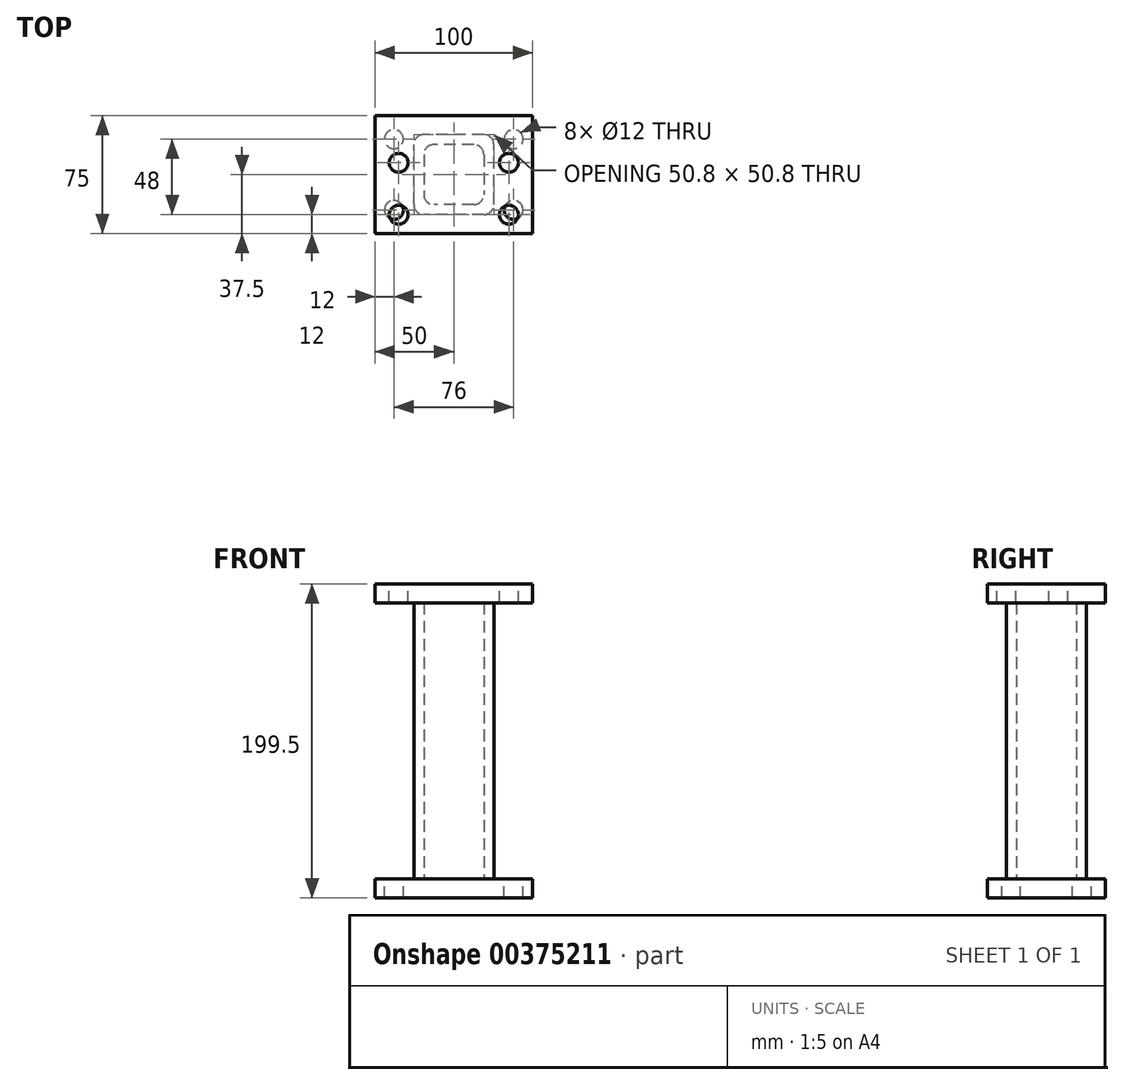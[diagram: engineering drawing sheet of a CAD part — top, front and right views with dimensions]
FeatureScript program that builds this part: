
annotation { "Feature Type Name" : "Feature", "Feature Type Description" : "" }
export const myFeature = defineFeature(function(context is Context, id is Id, definition is map)
    precondition{}
    {
        {
            var Q0;
            Q0=qCreatedBy(makeId("Top.planeOp"),FACE);
            var sketch = newSketch(context, id + "F0", { "sketchPlane" : qUnion([Q0])});
            skLineSegment(sketch, "E0.bottom", {"start": v(50, 37.5) * mm, "end": v(-50, 37.5) * mm});
            skLineSegment(sketch, "E0.top", {"start": v(50, -37.5) * mm, "end": v(-50, -37.5) * mm});
            skLineSegment(sketch, "E0.left", {"start": v(50, 37.5) * mm, "end": v(50, -37.5) * mm});
            skLineSegment(sketch, "E0.right", {"start": v(-50, 37.5) * mm, "end": v(-50, -37.5) * mm});
            skPoint(sketch, "E0.middle", {"position": v(0, 0) * mm});
            skSolve(sketch);
        }
        {
            var Q0;
            Q0=makeQuery(id+"F0.imprint","IMPRINT",FACE,{"disambiguationData":[TD([[makeQuery(id+"F0.imprint","IMPRINT",EDGE,{"derivedFrom":sQuery(id+"F0.wireOp",EDGE,"E0.bottom")}),1.0]])]});
            extrude(context, id + "F1", {"entities" : qUnion([Q0]), "depth" : -12 * mm});
        }
        {
            var Q0;
            Q0=makeQuery(id+"F1.opExtrude","CAP_FACE",FACE,{"disambiguationData":[OSD([sQuery(id+"F0.wireOp",EDGE,"E0.bottom"),sQuery(id+"F0.wireOp",EDGE,"E0.top"),sQuery(id+"F0.wireOp",EDGE,"E0.left"),sQuery(id+"F0.wireOp",EDGE,"E0.right")])],"isStart":true});
            var sketch = newSketch(context, id + "F2", { "sketchPlane" : qUnion([Q0])});
            skLineSegment(sketch, "E1.bottom", {"start": v(19.05, -25.4) * mm, "end": v(-19.05, -25.4) * mm});
            skLineSegment(sketch, "E1.top", {"start": v(19.05, 25.4) * mm, "end": v(-19.05, 25.4) * mm});
            skLineSegment(sketch, "E1.left", {"start": v(25.4, -19.05) * mm, "end": v(25.4, 19.05) * mm});
            skLineSegment(sketch, "E1.right", {"start": v(-25.4, -19.05) * mm, "end": v(-25.4, 19.05) * mm});
            skPoint(sketch, "E1.middle", {"position": v(0, 0) * mm});
            skPoint(sketch, "E2.visualSharp", {"position": v(-25.4, -25.4) * mm});
            skArc(sketch, "E2.filletArc", {"start": v(-25.4, -19.05) * mm, "mid": v(-23.54, -23.54) * mm, "end": v(-19.05, -25.4) * mm});
            skPoint(sketch, "E3.visualSharp", {"position": v(-25.4, 25.4) * mm});
            skArc(sketch, "E3.filletArc", {"start": v(-19.05, 25.4) * mm, "mid": v(-23.54, 23.54) * mm, "end": v(-25.4, 19.05) * mm});
            skPoint(sketch, "E4.visualSharp", {"position": v(25.4, 25.4) * mm});
            skArc(sketch, "E4.filletArc", {"start": v(25.4, 19.05) * mm, "mid": v(23.54, 23.54) * mm, "end": v(19.05, 25.4) * mm});
            skPoint(sketch, "E5.visualSharp", {"position": v(25.4, -25.4) * mm});
            skArc(sketch, "E5.filletArc", {"start": v(19.05, -25.4) * mm, "mid": v(23.54, -23.54) * mm, "end": v(25.4, -19.05) * mm});
            skLineSegment(sketch, "E6.bottom", {"start": v(12.7, 19.05) * mm, "end": v(-12.7, 19.05) * mm});
            skLineSegment(sketch, "E6.top", {"start": v(12.7, -19.05) * mm, "end": v(-12.7, -19.05) * mm});
            skLineSegment(sketch, "E6.left", {"start": v(19.05, 12.7) * mm, "end": v(19.05, -12.7) * mm});
            skLineSegment(sketch, "E6.right", {"start": v(-19.05, 12.7) * mm, "end": v(-19.05, -12.7) * mm});
            skArc(sketch, "E7.filletArc", {"start": v(-12.7, 19.05) * mm, "mid": v(-17.2, 17.2) * mm, "end": v(-19.05, 12.7) * mm});
            skArc(sketch, "E8.filletArc", {"start": v(19.05, 12.7) * mm, "mid": v(17.2, 17.2) * mm, "end": v(12.7, 19.05) * mm});
            skArc(sketch, "E9.filletArc", {"start": v(12.7, -19.05) * mm, "mid": v(17.2, -17.2) * mm, "end": v(19.05, -12.7) * mm});
            skArc(sketch, "E10.filletArc", {"start": v(-19.05, -12.7) * mm, "mid": v(-17.2, -17.2) * mm, "end": v(-12.7, -19.05) * mm});
            skSolve(sketch);
        }
        {
            var Q0;
            Q0=qSketchRegion(id+"F2",true);
            extrude(context, id + "F3", {"entities" : qUnion([Q0]), "operationType" : NewBodyOperationType.ADD, "depth" : 175.5 * mm});
        }
        {
            var Q0;
            {var subQ0=sQuery(id+"F0.wireOp",EDGE,"E0.left");var subQ1=sQuery(id+"F0.wireOp",EDGE,"E0.bottom");var subQ2=sQuery(id+"F0.wireOp",EDGE,"E0.right");var subQ3=sQuery(id+"F0.wireOp",EDGE,"E0.top");Q0=makeQuery(id+"F3.boolean.opBoolean","SPLIT",FACE,{"disambiguationData":[TD([makeQuery(id+"F1.opExtrude","SWEPT_FACE",FACE,{"disambiguationData":[OSD([subQ1])]})])],"derivedFrom":makeQuery(id+"F1.opExtrude","CAP_FACE",FACE,{"disambiguationData":[OSD([subQ1,subQ3,subQ0,subQ2])],"isStart":true})});}
            var sketch = newSketch(context, id + "F4", { "sketchPlane" : qUnion([Q0])});
            skLineSegment(sketch, "E11", {"start": v(-50, -37.5) * mm, "end": v(-38, -37.5) * mm, "construction": true});
            skLineSegment(sketch, "E12", {"start": v(-38, -37.5) * mm, "end": v(-38, -22.5) * mm, "construction": true});
            skLineSegment(sketch, "E13", {"start": v(-50, 37.5) * mm, "end": v(-38, 37.5) * mm, "construction": true});
            skLineSegment(sketch, "E14", {"start": v(-38, 37.5) * mm, "end": v(-38, 22.5) * mm, "construction": true});
            skLineSegment(sketch, "E15", {"start": v(50, 37.5) * mm, "end": v(38, 37.5) * mm, "construction": true});
            skLineSegment(sketch, "E16", {"start": v(50, -37.5) * mm, "end": v(38, -37.5) * mm, "construction": true});
            skLineSegment(sketch, "E17", {"start": v(38, -37.5) * mm, "end": v(38, -22.5) * mm, "construction": true});
            skLineSegment(sketch, "E18", {"start": v(38, 37.5) * mm, "end": v(38, 22.5) * mm, "construction": true});
            skSolve(sketch);
        }
        {
            var Q0;
            Q0=makeQuery(id+"F3.opExtrude","CAP_FACE",FACE,{"disambiguationData":[OSD([sQuery(id+"F2.wireOp",EDGE,"E1.bottom"),sQuery(id+"F2.wireOp",EDGE,"E1.top"),sQuery(id+"F2.wireOp",EDGE,"E1.left"),sQuery(id+"F2.wireOp",EDGE,"E1.right"),sQuery(id+"F2.wireOp",EDGE,"E2.filletArc"),sQuery(id+"F2.wireOp",EDGE,"E3.filletArc"),sQuery(id+"F2.wireOp",EDGE,"E4.filletArc"),sQuery(id+"F2.wireOp",EDGE,"E5.filletArc"),sQuery(id+"F2.wireOp",EDGE,"E6.bottom"),sQuery(id+"F2.wireOp",EDGE,"E6.top"),sQuery(id+"F2.wireOp",EDGE,"E6.left"),sQuery(id+"F2.wireOp",EDGE,"E6.right"),sQuery(id+"F2.wireOp",EDGE,"E7.filletArc"),sQuery(id+"F2.wireOp",EDGE,"E8.filletArc"),sQuery(id+"F2.wireOp",EDGE,"E9.filletArc"),sQuery(id+"F2.wireOp",EDGE,"E10.filletArc")])],"isStart":false});
            var sketch = newSketch(context, id + "F5", { "sketchPlane" : qUnion([Q0])});
            skLineSegment(sketch, "E19.bottom", {"start": v(50, -37.5) * mm, "end": v(-50, -37.5) * mm});
            skLineSegment(sketch, "E19.top", {"start": v(50, 37.5) * mm, "end": v(-50, 37.5) * mm});
            skLineSegment(sketch, "E19.left", {"start": v(50, -37.5) * mm, "end": v(50, 37.5) * mm});
            skLineSegment(sketch, "E19.right", {"start": v(-50, -37.5) * mm, "end": v(-50, 37.5) * mm});
            skPoint(sketch, "E19.middle", {"position": v(0, 0) * mm});
            skSolve(sketch);
        }
        {
            var Q0;
            Q0=makeQuery(id+"F5.imprint","IMPRINT",FACE,{"disambiguationData":[TD([[makeQuery(id+"F5.imprint","IMPRINT",EDGE,{"derivedFrom":makeQuery(id+"F3.opExtrude","CAP_EDGE",EDGE,{"disambiguationData":[OSD([sQuery(id+"F2.wireOp",EDGE,"E6.bottom")])],"isStart":false})}),1.0]])]});
            var Q1;
            Q1=makeQuery(id+"F5.imprint","IMPRINT",FACE,{"disambiguationData":[TD([[makeQuery(id+"F5.imprint","IMPRINT",EDGE,{"derivedFrom":sQuery(id+"F5.wireOp",EDGE,"E19.bottom")}),-1.0]])]});
            var Q2;
            Q2=makeQuery(id+"F5.imprint","IMPRINT",FACE,{"disambiguationData":[TD([[makeQuery(id+"F5.imprint","IMPRINT",EDGE,{"derivedFrom":makeQuery(id+"F3.opExtrude","CAP_EDGE",EDGE,{"disambiguationData":[OSD([sQuery(id+"F2.wireOp",EDGE,"E1.bottom")])],"isStart":false})}),-1.0]])]});
            extrude(context, id + "F6", {"entities" : qUnion([Q0, Q1, Q2]), "operationType" : NewBodyOperationType.ADD, "depth" : 12 * mm});
        }
        {
            var Q0;
            Q0=sQuery(id+"F4.wireOp",VERTEX,"E14.end");
            var Q1;
            Q1=sQuery(id+"F4.wireOp",VERTEX,"E18.end");
            var Q2;
            Q2=sQuery(id+"F4.wireOp",VERTEX,"E17.end");
            var Q3;
            Q3=sQuery(id+"F4.wireOp",VERTEX,"E12.end");
            var Q4;
            Q4=makeQuery(id+"F1.opExtrude","SWEPT_BODY",BODY,{"disambiguationData":[OSD([sQuery(id+"F0.wireOp",EDGE,"E0.bottom"),sQuery(id+"F0.wireOp",EDGE,"E0.top"),sQuery(id+"F0.wireOp",EDGE,"E0.left"),sQuery(id+"F0.wireOp",EDGE,"E0.right")])]});
            hole(context, id + "F7", {"style" : HoleStyle.SIMPLE, "endStyle" : HoleEndStyle.THROUGH, "holeDiameter" : 12 * mm, "isTappedThrough" : true, "tappedDepth" : 12 * mm, "tapClearance" : 3, "locations" : qUnion([Q0, Q1, Q2, Q3]), "scope" : qUnion([Q4])});
        }
        {
            var Q0;
            Q0=makeQuery(id+"F6.opExtrude","CAP_FACE",FACE,{"disambiguationData":[OSD([sQuery(id+"F5.wireOp",EDGE,"E19.bottom"),sQuery(id+"F5.wireOp",EDGE,"E19.top"),sQuery(id+"F5.wireOp",EDGE,"E19.left"),sQuery(id+"F5.wireOp",EDGE,"E19.right")])],"isStart":false});
            var sketch = newSketch(context, id + "F8", { "sketchPlane" : qUnion([Q0])});
            skLineSegment(sketch, "E20", {"start": v(50, -37.5) * mm, "end": v(35, -37.5) * mm, "construction": true});
            skLineSegment(sketch, "E21", {"start": v(35, -37.5) * mm, "end": v(35, -25.5) * mm, "construction": true});
            skLineSegment(sketch, "E22", {"start": v(-50, -37.5) * mm, "end": v(-50, -25.5) * mm, "construction": true});
            skLineSegment(sketch, "E23", {"start": v(-50, -25.5) * mm, "end": v(-35, -25.5) * mm, "construction": true});
            skLineSegment(sketch, "E24", {"start": v(-35, -25.5) * mm, "end": v(-35, 7.5) * mm, "construction": true});
            skLineSegment(sketch, "E25", {"start": v(35, -25.5) * mm, "end": v(35, 7.5) * mm, "construction": true});
            skSolve(sketch);
        }
        {
            var Q0;
            Q0=sQuery(id+"F8.wireOp",VERTEX,"E24.end");
            var Q1;
            Q1=sQuery(id+"F8.wireOp",VERTEX,"E24.start");
            var Q2;
            Q2=sQuery(id+"F8.wireOp",VERTEX,"E25.start");
            var Q3;
            Q3=sQuery(id+"F8.wireOp",VERTEX,"E25.end");
            var Q4;
            Q4=makeQuery(id+"F1.opExtrude","SWEPT_BODY",BODY,{"disambiguationData":[OSD([sQuery(id+"F0.wireOp",EDGE,"E0.bottom"),sQuery(id+"F0.wireOp",EDGE,"E0.top"),sQuery(id+"F0.wireOp",EDGE,"E0.left"),sQuery(id+"F0.wireOp",EDGE,"E0.right")])]});
            hole(context, id + "F9", {"style" : HoleStyle.SIMPLE, "endStyle" : HoleEndStyle.BLIND, "holeDiameter" : 12 * mm, "holeDepth" : 12 * mm, "isTappedThrough" : true, "tappedDepth" : 12 * mm, "tapClearance" : 3, "locations" : qUnion([Q0, Q1, Q2, Q3]), "scope" : qUnion([Q4])});
        }
    });
